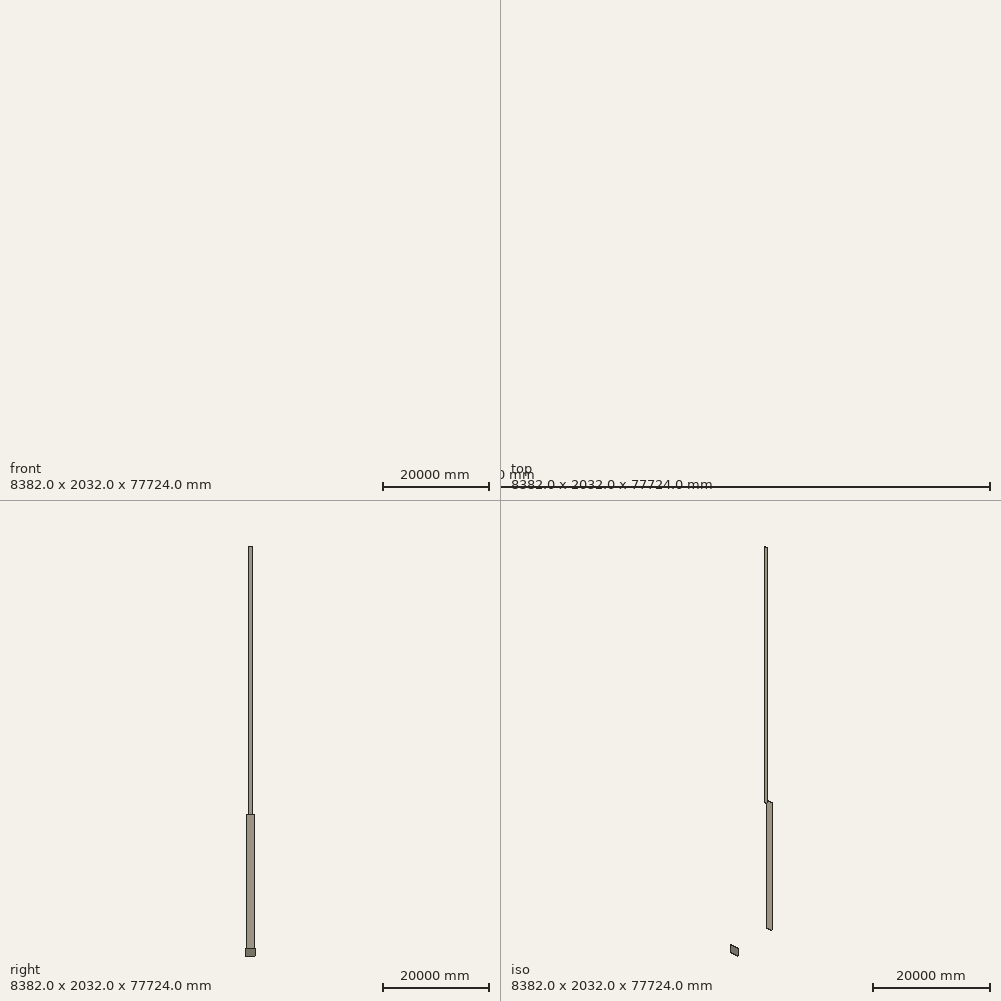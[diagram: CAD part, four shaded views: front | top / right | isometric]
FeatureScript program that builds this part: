
annotation { "Feature Type Name" : "Feature", "Feature Type Description" : "" }
export const myFeature = defineFeature(function(context is Context, id is Id, definition is map)
    precondition{}
    {
        {
            var Q0;
            Q0=qCreatedBy(makeId("Front.planeOp"),FACE);
            var sketch = newSketch(context, id + "F0", { "sketchPlane" : qUnion([Q0])});
            skLineSegment(sketch, "E0.bottom", {"start": v(0, 0) * mm, "end": v(7620, 0) * mm});
            skLineSegment(sketch, "E0.top", {"start": v(0, -1524) * mm, "end": v(7620, -1524) * mm});
            skLineSegment(sketch, "E0.left", {"start": v(0, 0) * mm, "end": v(0, -1524) * mm});
            skLineSegment(sketch, "E0.right", {"start": v(7620, 0) * mm, "end": v(7620, -1524) * mm});
            skLineSegment(sketch, "E1.MirrorCS", {"start": v(0, -1524) * mm, "end": v(-7620, -1524) * mm});
            skLineSegment(sketch, "E2.MirrorCS", {"start": v(-7620, 0) * mm, "end": v(-7620, -1524) * mm});
            skLineSegment(sketch, "E3.MirrorCS", {"start": v(0, 0) * mm, "end": v(-7620, 0) * mm});
            skLineSegment(sketch, "E4.bottom", {"start": v(0, 0) * mm, "end": v(762, 0) * mm});
            skLineSegment(sketch, "E4.top", {"start": v(0, 25400) * mm, "end": v(762, 25400) * mm});
            skLineSegment(sketch, "E4.left", {"start": v(0, 0) * mm, "end": v(0, 25400) * mm});
            skLineSegment(sketch, "E4.right", {"start": v(762, 0) * mm, "end": v(762, 25400) * mm});
            skLineSegment(sketch, "E5.MirrorCS", {"start": v(0, 0) * mm, "end": v(-762, 0) * mm});
            skLineSegment(sketch, "E6.MirrorCS", {"start": v(0, 25400) * mm, "end": v(-762, 25400) * mm});
            skLineSegment(sketch, "E7.MirrorCS", {"start": v(-762, 0) * mm, "end": v(-762, 25400) * mm});
            skPoint(sketch, "E8.oppositeSnap0", {"position": v(381, 25400) * mm});
            skLineSegment(sketch, "E8.bottom", {"start": v(0, 25400) * mm, "end": v(381, 25400) * mm});
            skLineSegment(sketch, "E8.top", {"start": v(0, 76200) * mm, "end": v(381, 76200) * mm});
            skLineSegment(sketch, "E8.left", {"start": v(0, 25400) * mm, "end": v(0, 76200) * mm});
            skLineSegment(sketch, "E8.right", {"start": v(381, 25400) * mm, "end": v(381, 76200) * mm});
            skLineSegment(sketch, "E9.MirrorCS", {"start": v(0, 25400) * mm, "end": v(-381, 25400) * mm});
            skLineSegment(sketch, "E10.MirrorCS", {"start": v(-381, 25400) * mm, "end": v(-381, 76200) * mm});
            skLineSegment(sketch, "E11.MirrorCS", {"start": v(0, 76200) * mm, "end": v(-381, 76200) * mm});
            skPoint(sketch, "E12.MirrorP", {"position": v(-381, 25400) * mm});
            skSolve(sketch);
        }
        {
            var Q0;
            Q0=sQuery(id+"F0.wireOp",EDGE,"E2.MirrorCS");
            extrude(context, id + "F1", {"bodyType" : ToolBodyType.SURFACE, "surfaceEntities" : qUnion([Q0]), "endBound" : BoundingType.SYMMETRIC, "depth" : 2032 * mm, "offsetDistance" : 25.4 * mm});
        }
        {
            var Q0;
            Q0=sQuery(id+"F0.wireOp",EDGE,"E4.right");
            extrude(context, id + "F2", {"bodyType" : ToolBodyType.SURFACE, "surfaceEntities" : qUnion([Q0]), "endBound" : BoundingType.SYMMETRIC, "depth" : 1524 * mm, "offsetDistance" : 25.4 * mm});
        }
        {
            var Q0;
            Q0=sQuery(id+"F0.wireOp",EDGE,"E8.left");
            extrude(context, id + "F3", {"bodyType" : ToolBodyType.SURFACE, "surfaceEntities" : qUnion([Q0]), "endBound" : BoundingType.SYMMETRIC, "depth" : 762 * mm, "offsetDistance" : 25.4 * mm});
        }
    });
